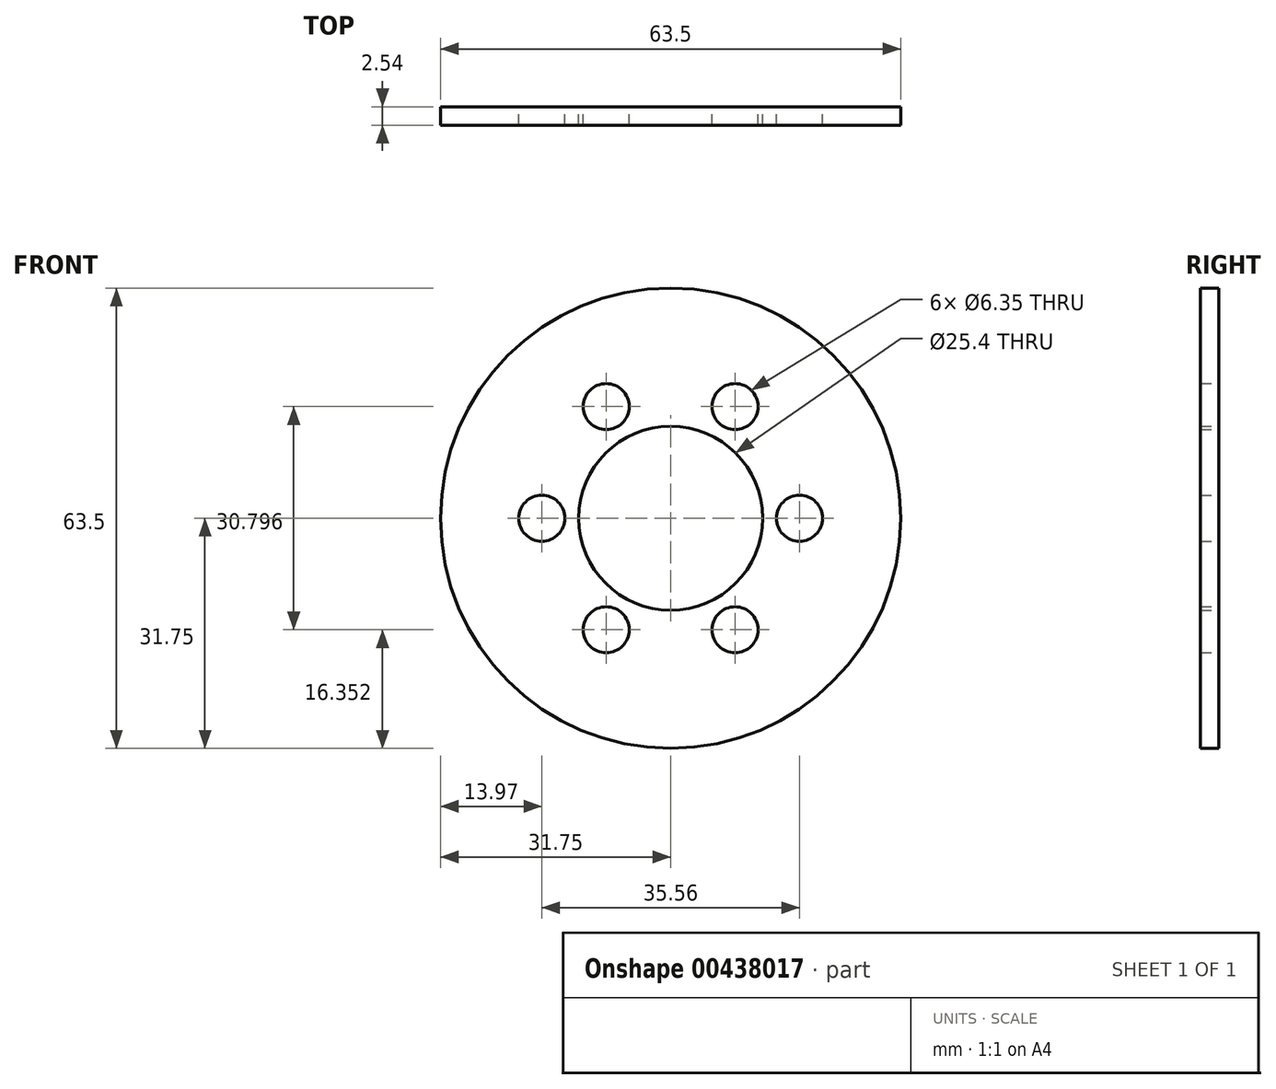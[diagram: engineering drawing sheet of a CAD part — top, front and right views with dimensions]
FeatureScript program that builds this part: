
annotation { "Feature Type Name" : "Feature", "Feature Type Description" : "" }
export const myFeature = defineFeature(function(context is Context, id is Id, definition is map)
    precondition{}
    {
        {
            var Q0;
            Q0=qCreatedBy(makeId("Front.planeOp"),FACE);
            var sketch = newSketch(context, id + "F0", { "sketchPlane" : qUnion([Q0])});
            skCircle(sketch, "E0", {"center": v(0, 0) * mm, "radius": 31.75 * mm});
            skCircle(sketch, "E1", {"center": v(0, 0) * mm, "radius": 12.7 * mm});
            skCircle(sketch, "E2", {"center": v(17.78, 0) * mm, "radius": 3.18 * mm});
            skCircle(sketch, "E3.1.0", {"center": v(8.9, 15.4) * mm, "radius": 3.18 * mm});
            skCircle(sketch, "E3.2.0", {"center": v(-8.89, 15.4) * mm, "radius": 3.18 * mm});
            skCircle(sketch, "E3.3.0", {"center": v(-17.78, 0) * mm, "radius": 3.18 * mm});
            skCircle(sketch, "E3.4.0", {"center": v(-8.9, -15.4) * mm, "radius": 3.18 * mm});
            skCircle(sketch, "E3.5.0", {"center": v(8.9, -15.4) * mm, "radius": 3.18 * mm});
            skSolve(sketch);
        }
        {
            var Q0;
            Q0=makeQuery(id+"F0.imprint","IMPRINT",FACE,{"disambiguationData":[TD([[makeQuery(id+"F0.imprint","IMPRINT",EDGE,{"derivedFrom":sQuery(id+"F0.wireOp",EDGE,"E0")}),1.0]])]});
            extrude(context, id + "F1", {"entities" : qUnion([Q0]), "depth" : 2.54 * mm});
        }
    });
